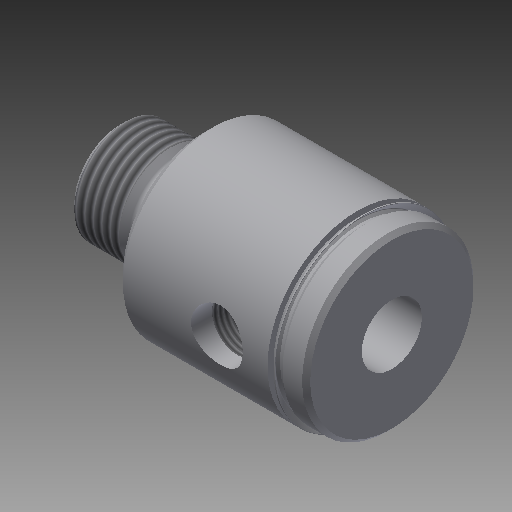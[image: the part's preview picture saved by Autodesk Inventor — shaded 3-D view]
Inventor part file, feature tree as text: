
AUTODESK INVENTOR PART (.ipt)
format: ipt  version: 2019 (Build 230136000, 136)  size: 300,032 bytes
history: native  units: in
note: dims shown in document units (in); Inventor stores cm internally (conversion verified against a paired STEP export)
features: other x119, sketch x5, revolve x4, thread x2, hole x1
ambient origin geometry x8: Origin, YZ Plane, XZ Plane, XY Plane, X Axis, Y Axis, Z Axis, Center Point
bodies: Solid1 (feature_tree)
feature tree (131):
  revolve  "Revolution1"  [1 undecoded]
  thread  "Thread1"  [1 undecoded]
  revolve  "Revolution2"  Angle=360.0deg
  hole  "Hole1"  [1 undecoded]
  revolve  "Revolution3"  [1 undecoded]
  thread  "Thread2"  [1 undecoded]
  revolve  "Revolution4"  [1 undecoded]
  other  "dp1_XY"
  other  "dp1_YZ"
  other  "dp1_ZX"
  other  "dp1_X"
  other  "dp1_Y"
  other  "dp1_Z"
  other  "dp1_Center"
  other  "dp2_XY"
  other  "dp2_YZ"
  other  "dp2_ZX"
  other  "dp2_X"
  other  "dp2_Y"
  other  "dp2_Z"
  other  "dp2_Center"
  other  "hh_XY"
  other  "hh_YZ"
  other  "hh_ZX"
  other  "hh_X"
  other  "hh_Y"
  other  "hh_Z"
  other  "hh_Center"
  other  "port_XY"
  other  "port_YZ"
  other  "port_ZX"
  other  "port_X"
  other  "port_Y"
  other  "port_Z"
  other  "port_Center"
  other  "rod_guide_XY"
  other  "rod_guide_YZ"
  other  "rod_guide_ZX"
  other  "rod_guide_X"
  other  "rod_guide_Y"
  other  "rod_guide_Z"
  other  "rod_guide_Center"
  other  "s1_XY"
  other  "s1_YZ"
  other  "s1_ZX"
  other  "s1_X"
  other  "s1_Y"
  other  "s1_Z"
  other  "s1_Center"
  other  "s2_XY"
  other  "s2_YZ"
  other  "s2_ZX"
  other  "s2_X"
  other  "s2_Y"
  other  "s2_Z"
  other  "s2_Center"
  other  "t1_XY"
  other  "t1_YZ"
  other  "t1_ZX"
  other  "t1_X"
  other  "t1_Y"
  other  "t1_Z"
  other  "t1_Center"
  other  "t111_XY"
  other  "t111_YZ"
  other  "t111_ZX"
  other  "t111_X"
  other  "t111_Y"
  other  "t111_Z"
  other  "t111_Center"
  other  "to_foot_bracket_XY"
  other  "to_foot_bracket_YZ"
  other  "to_foot_bracket_ZX"
  other  "to_foot_bracket_X"
  other  "to_foot_bracket_Y"
  other  "to_foot_bracket_Z"
  other  "to_foot_bracket_Center"
  other  "to_nut_XY"
  other  "to_nut_YZ"
  other  "to_nut_ZX"
  other  "to_nut_X"
  other  "to_nut_Y"
  other  "to_nut_Z"
  other  "to_nut_Center"
  other  "to_rod_XY"
  other  "to_rod_YZ"
  other  "to_rod_ZX"
  other  "to_rod_X"
  other  "to_rod_Y"
  other  "to_rod_Z"
  other  "to_rod_Center"
  other  "to_screw_XY"
  other  "to_screw_YZ"
  other  "to_screw_ZX"
  other  "to_screw_X"
  other  "to_screw_Y"
  other  "to_screw_Z"
  other  "to_screw_Center"
  other  "to_trunnion_brackets_XY"
  other  "to_trunnion_brackets_YZ"
  other  "to_trunnion_brackets_ZX"
  other  "to_trunnion_brackets_X"
  other  "to_trunnion_brackets_Y"
  other  "to_trunnion_brackets_Z"
  other  "to_trunnion_brackets_Center"
  other  "to_trunnion_brackets1_XY"
  other  "to_trunnion_brackets1_YZ"
  other  "to_trunnion_brackets1_ZX"
  other  "to_trunnion_brackets1_X"
  other  "to_trunnion_brackets1_Y"
  other  "to_trunnion_brackets1_Z"
  other  "to_trunnion_brackets1_Center"
  other  "to_trunnion_brackets2_XY"
  other  "to_trunnion_brackets2_YZ"
  other  "to_trunnion_brackets2_ZX"
  other  "to_trunnion_brackets2_X"
  other  "to_trunnion_brackets2_Y"
  other  "to_trunnion_brackets2_Z"
  other  "to_trunnion_brackets2_Center"
  other  "to_tube_XY"
  other  "to_tube_YZ"
  other  "to_tube_ZX"
  other  "to_tube_X"
  other  "to_tube_Y"
  other  "to_tube_Z"
  other  "to_tube_Center"
  sketch  "Sketch_2"  dims[d0=360.0deg d1=0.3315in d2=0.0in d3=360.0deg]
  sketch  "Sketch_3"  dims[d4=0.442in d5=0.75in d6=0.502in d7=0.25in d8=90.0deg d9=2.0in d10=0.0in d11=360.0deg]
  sketch  "Sketch3"  dims[d12=0.2251in d13=0.0in d14=360.0deg]
  sketch  "Sketch_40"  dims[d15=0.0in d16=0.0in d17=0.0in d18=0.0in d19=0.0in d20=0.0in]
  sketch  "Sketch_47"
note: 6 required parameter values undecoded (feature->parameter linkage not recoverable at this tier; creation-order binding heuristic only, values carry confidence <= 0.55)